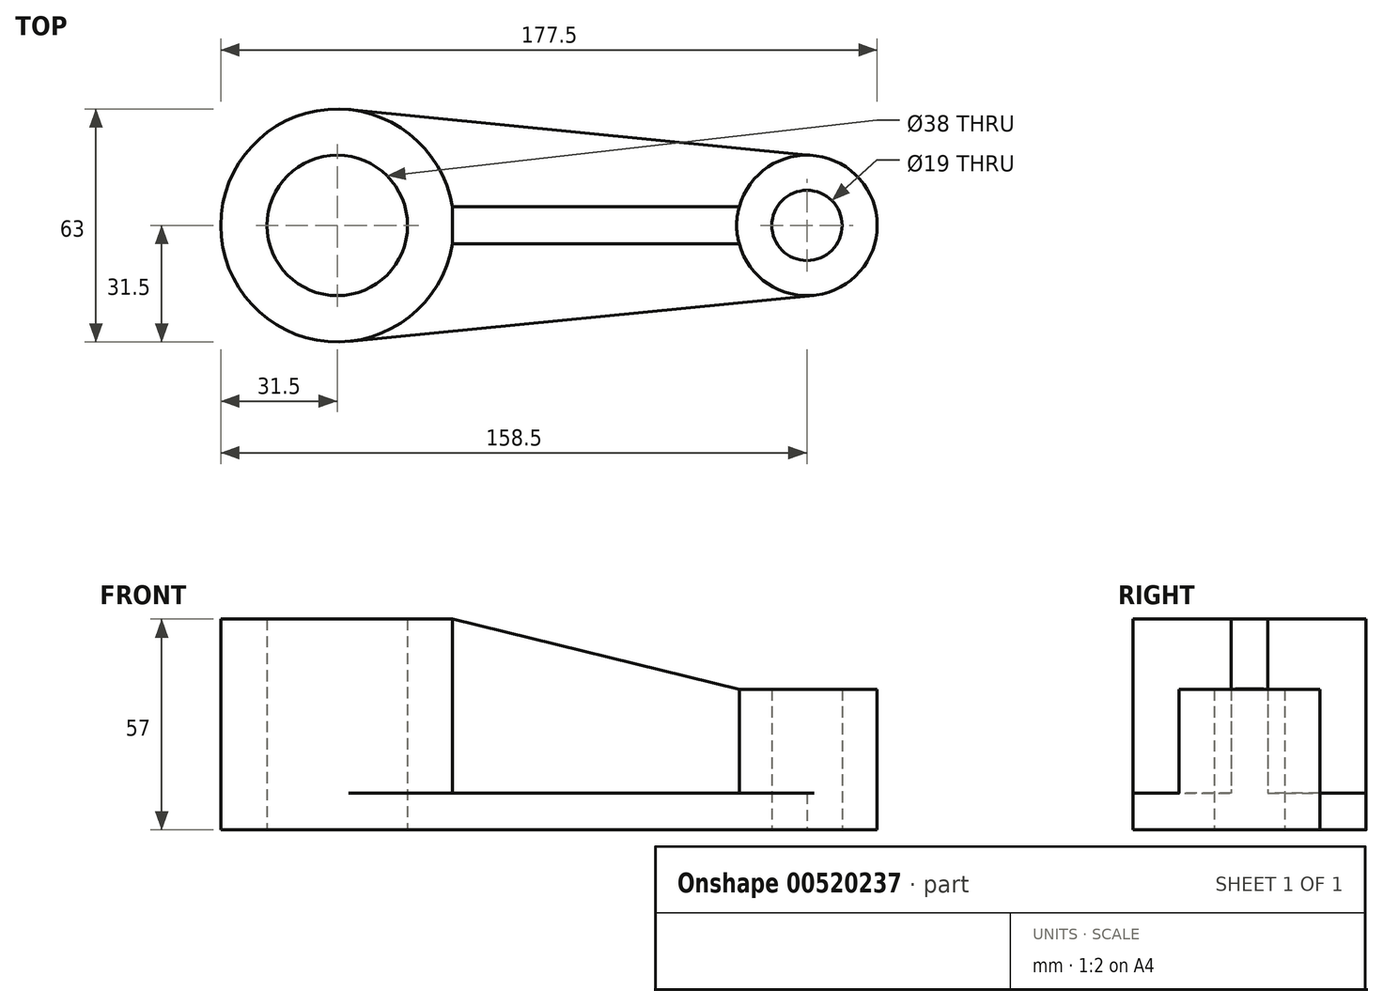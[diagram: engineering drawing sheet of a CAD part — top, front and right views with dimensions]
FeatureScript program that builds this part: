
annotation { "Feature Type Name" : "Feature", "Feature Type Description" : "" }
export const myFeature = defineFeature(function(context is Context, id is Id, definition is map)
    precondition{}
    {
        {
            var Q0;
            Q0=qCreatedBy(makeId("Top.planeOp"),FACE);
            var sketch = newSketch(context, id + "F0", { "sketchPlane" : qUnion([Q0])});
            skCircle(sketch, "E0", {"center": v(0, 0) * mm, "radius": 9.5 * mm});
            skCircle(sketch, "E1", {"center": v(0, 0) * mm, "radius": 14.01 * mm, "construction": true});
            skCircle(sketch, "E2", {"center": v(0, 0) * mm, "radius": 19 * mm});
            skLineSegment(sketch, "E3", {"start": v(0, 0) * mm, "end": v(-127, 0) * mm, "construction": true});
            skCircle(sketch, "E4", {"center": v(-127, 0) * mm, "radius": 19 * mm});
            skLineSegment(sketch, "E5", {"start": v(-95.9, 5) * mm, "end": v(-18.33, 5) * mm});
            skLineSegment(sketch, "E6", {"start": v(-18.33, -5) * mm, "end": v(-95.9, -5) * mm});
            skCircle(sketch, "E7", {"center": v(-127, 0) * mm, "radius": 31.5 * mm});
            skLineSegment(sketch, "E8", {"start": v(1.87, -18.9) * mm, "end": v(-123.9, -31.35) * mm});
            skLineSegment(sketch, "E9", {"start": v(0, 19) * mm, "end": v(-123.88, 31.34) * mm});
            skPoint(sketch, "E10.orphan", {"position": v(0, -19.1) * mm});
            skSolve(sketch);
        }
        {
            var Q0;
            {var subQ1=sQuery(id+"F0.wireOp",EDGE,"E4");var subQ7=sQuery(id+"F0.wireOp",EDGE,"E5");var subQ9=makeQuery(id+"F0.imprint","INTERSECT",VERTEX,{"derivedFrom":[subQ1,subQ7]});Q0=makeQuery(id+"F0.imprint","IMPRINT",FACE,{"disambiguationData":[TD([[makeQuery(id+"F0.imprint","IMPRINT",EDGE,{"disambiguationData":[TD([[subQ9,-1.0]])],"derivedFrom":subQ1}),-1.0]])]});}
            extrude(context, id + "F1", {"entities" : qUnion([Q0]), "depth" : 57 * mm, "offsetDistance" : 25 * mm});
        }
        {
            var Q0;
            {var subQ0=sQuery(id+"F0.wireOp",EDGE,"E6");Q0=makeQuery(id+"F0.imprint","IMPRINT",FACE,{"disambiguationData":[TD([[makeQuery(id+"F0.imprint","IMPRINT",EDGE,{"derivedFrom":subQ0}),1.0]])]});}
            var Q1;
            {var subQ0=sQuery(id+"F0.wireOp",EDGE,"E5");Q1=makeQuery(id+"F0.imprint","IMPRINT",FACE,{"disambiguationData":[TD([[makeQuery(id+"F0.imprint","IMPRINT",EDGE,{"derivedFrom":subQ0}),1.0]])]});}
            extrude(context, id + "F2", {"entities" : qUnion([Q0, Q1]), "operationType" : NewBodyOperationType.ADD, "depth" : 10 * mm, "offsetDistance" : 25 * mm});
        }
        {
            var Q0;
            Q0=makeQuery(id+"F0.imprint","IMPRINT",FACE,{"disambiguationData":[TD([[makeQuery(id+"F0.imprint","IMPRINT",EDGE,{"derivedFrom":sQuery(id+"F0.wireOp",EDGE,"E0")}),-1.0]])]});
            extrude(context, id + "F3", {"entities" : qUnion([Q0]), "operationType" : NewBodyOperationType.ADD, "depth" : 38 * mm, "offsetDistance" : 25 * mm});
        }
        {
            var Q0;
            Q0=qCreatedBy(makeId("Top.planeOp"),FACE);
            var sketch = newSketch(context, id + "F4", { "sketchPlane" : qUnion([Q0])});
            skSolve(sketch);
        }
        {
            var Q0;
            Q0 = qSketchRegion(id + "F4", true);
            var Q1;
            {var subQ0=sQuery(id+"F0.wireOp",EDGE,"E5");Q1=makeQuery(id+"F0.imprint","IMPRINT",FACE,{"disambiguationData":[TD([[makeQuery(id+"F0.imprint","IMPRINT",EDGE,{"derivedFrom":subQ0}),-1.0]])]});}
            extrude(context, id + "F5", {"entities" : qUnion([Q0, Q1]), "operationType" : NewBodyOperationType.ADD, "depth" : 57 * mm, "offsetDistance" : 25 * mm});
        }
        {
            var Q0;
            Q0=makeQuery(id+"F5.opExtrude","SWEPT_FACE",FACE,{"disambiguationData":[OSD([sQuery(id+"F0.wireOp",EDGE,"E6")])]});
            var sketch = newSketch(context, id + "F6", { "sketchPlane" : qUnion([Q0])});
            skLineSegment(sketch, "E11", {"start": v(-95.9, 57) * mm, "end": v(-18.33, 38) * mm});
            skLineSegment(sketch, "E12", {"start": v(-18.33, 38) * mm, "end": v(-18.33, 57) * mm});
            skLineSegment(sketch, "E13", {"start": v(-18.33, 57) * mm, "end": v(-95.9, 57) * mm});
            skSolve(sketch);
        }
        {
            var Q0;
            Q0=makeQuery(id+"F6.imprint","IMPRINT",FACE,{"disambiguationData":[TD([[makeQuery(id+"F6.imprint","IMPRINT",EDGE,{"derivedFrom":sQuery(id+"F6.wireOp",EDGE,"E11")}),1.0]])]});
            extrude(context, id + "F7", {"entities" : qUnion([Q0]), "operationType" : NewBodyOperationType.REMOVE, "endBound" : BoundingType.THROUGH_ALL, "oppositeDirection" : true, "depth" : 25 * mm, "offsetDistance" : 25 * mm});
        }
    });
